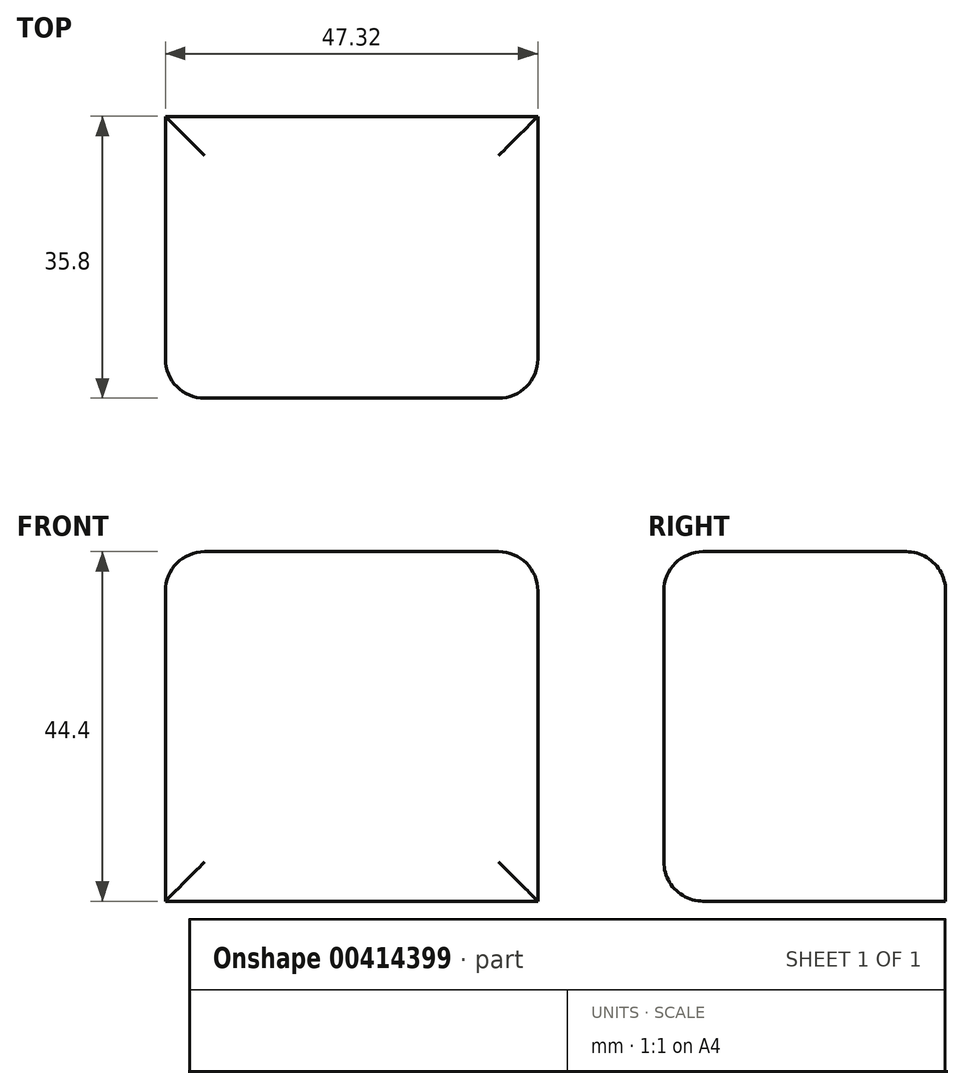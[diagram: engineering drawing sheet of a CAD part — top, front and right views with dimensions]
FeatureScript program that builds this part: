
annotation { "Feature Type Name" : "Feature", "Feature Type Description" : "" }
export const myFeature = defineFeature(function(context is Context, id is Id, definition is map)
    precondition{}
    {
        {
            var Q0;
            Q0=qCreatedBy(makeId("Top.planeOp"),FACE);
            var sketch = newSketch(context, id + "F0", { "sketchPlane" : qUnion([Q0])});
            skLineSegment(sketch, "E0.bottom", {"start": v(0, 0) * mm, "end": v(47.32, 0) * mm});
            skLineSegment(sketch, "E0.top", {"start": v(0, 35.8) * mm, "end": v(47.32, 35.8) * mm});
            skLineSegment(sketch, "E0.left", {"start": v(0, 0) * mm, "end": v(0, 35.8) * mm});
            skLineSegment(sketch, "E0.right", {"start": v(47.32, 0) * mm, "end": v(47.32, 35.8) * mm});
            skSolve(sketch);
        }
        {
            var Q0;
            Q0=makeQuery(id+"F0.imprint","IMPRINT",FACE,{"disambiguationData":[TD([[makeQuery(id+"F0.imprint","IMPRINT",EDGE,{"derivedFrom":sQuery(id+"F0.wireOp",EDGE,"E0.bottom")}),1.0]])]});
            extrude(context, id + "F1", {"entities" : qUnion([Q0]), "depth" : 44.4 * mm});
        }
        {
            var Q0;
            Q0=makeQuery(id+"F1.opExtrude","SWEPT_FACE",FACE,{"disambiguationData":[OSD([sQuery(id+"F0.wireOp",EDGE,"E0.bottom")])]});
            var Q1;
            Q1=makeQuery(id+"F1.opExtrude","CAP_FACE",FACE,{"disambiguationData":[OSD([sQuery(id+"F0.wireOp",EDGE,"E0.bottom"),sQuery(id+"F0.wireOp",EDGE,"E0.top"),sQuery(id+"F0.wireOp",EDGE,"E0.left"),sQuery(id+"F0.wireOp",EDGE,"E0.right")])],"isStart":false});
            fillet(context, id + "F2", {"entities" : qUnion([Q0, Q1]), "radius" : 5 * mm, "tangentPropagation" : true, "allowEdgeOverflow" : false});
        }
    });
